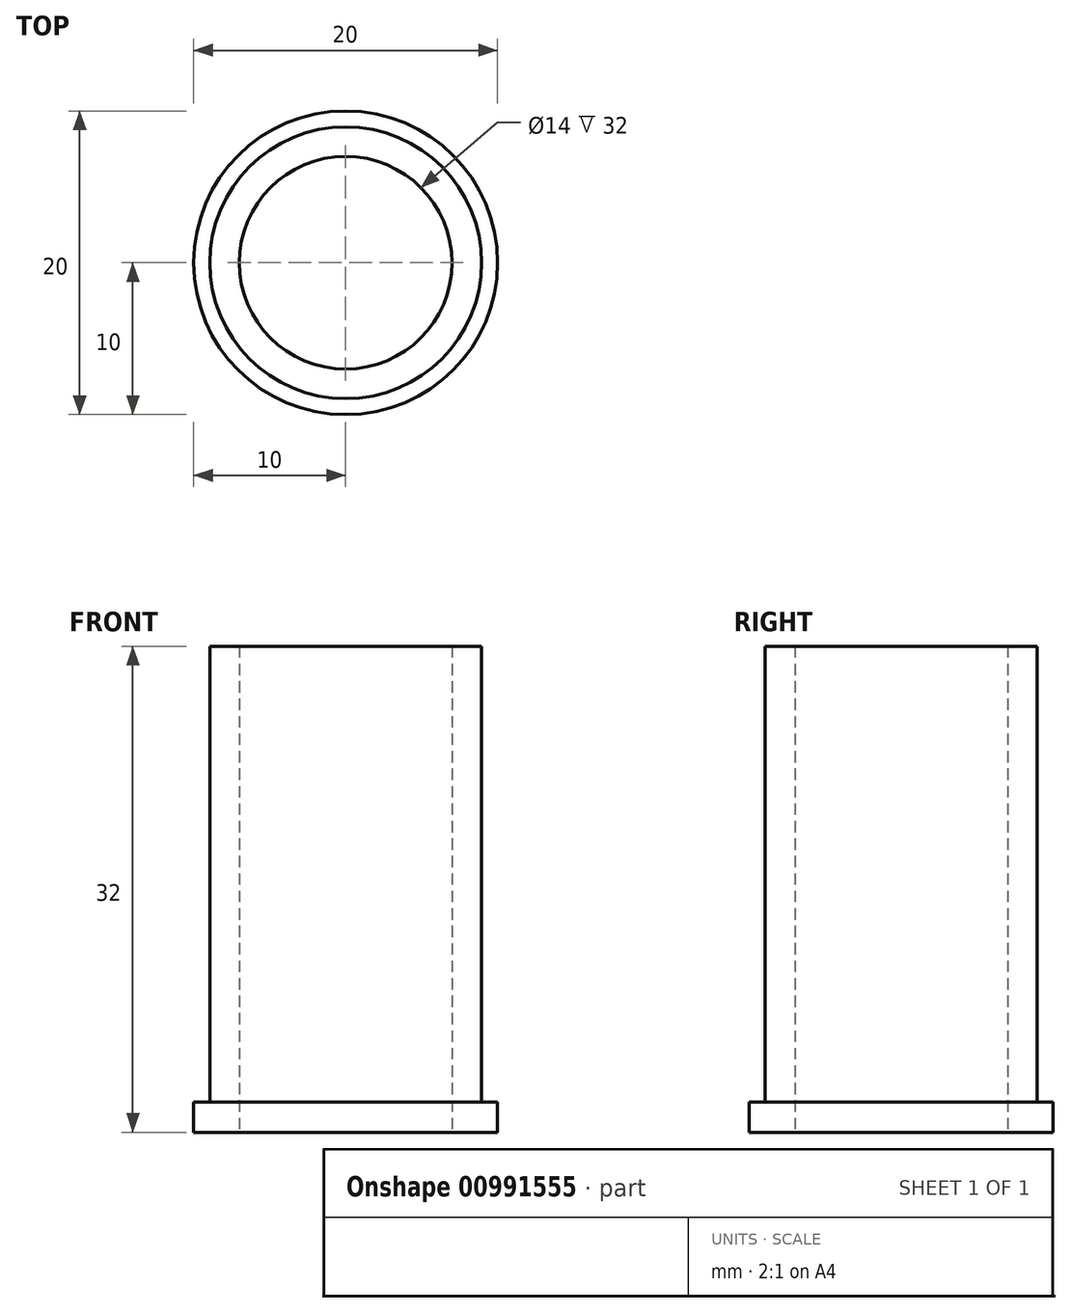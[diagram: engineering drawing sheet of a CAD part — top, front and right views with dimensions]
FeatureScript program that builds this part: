
annotation { "Feature Type Name" : "Feature", "Feature Type Description" : "" }
export const myFeature = defineFeature(function(context is Context, id is Id, definition is map)
    precondition{}
    {
        {
            var Q0;
            Q0=qCreatedBy(makeId("Top.planeOp"),FACE);
            var sketch = newSketch(context, id + "F0", { "sketchPlane" : qUnion([Q0]), "disableImprinting" : false});
            skCircle(sketch, "E0", {"center": v(0, 0) * mm, "radius": 8.95 * mm});
            skCircle(sketch, "E1", {"center": v(0, 0) * mm, "radius": 7 * mm});
            skSolve(sketch);
        }
        {
            var Q0;
            Q0=makeQuery(id+"F0.imprint","IMPRINT",FACE,{"disambiguationData":[TD([[makeQuery(id+"F0.imprint","IMPRINT",EDGE,{"derivedFrom":sQuery(id+"F0.wireOp",EDGE,"E0")}),1.0]])]});
            extrude(context, id + "F1", {"entities" : qUnion([Q0]), "depth" : 30 * mm, "offsetDistance" : 25 * mm});
        }
        {
            var Q0;
            Q0=makeQuery(id+"F1.opExtrude","CAP_FACE",FACE,{"disambiguationData":[OSD([sQuery(id+"F0.wireOp",EDGE,"E0"),sQuery(id+"F0.wireOp",EDGE,"E1")])],"isStart":true});
            var sketch = newSketch(context, id + "F2", { "sketchPlane" : qUnion([Q0])});
            skCircle(sketch, "E2", {"center": v(0, 0) * mm, "radius": 7 * mm});
            skCircle(sketch, "E3", {"center": v(0, 0) * mm, "radius": 10 * mm});
            skSolve(sketch);
        }
        {
            var Q0;
            Q0=makeQuery(id+"F2.imprint","IMPRINT",FACE,{"disambiguationData":[TD([[makeQuery(id+"F2.imprint","IMPRINT",EDGE,{"derivedFrom":sQuery(id+"F2.wireOp",EDGE,"E3")}),1.0]])]});
            var Q1;
            Q1=makeQuery(id+"F2.imprint","IMPRINT",FACE,{"disambiguationData":[TD([[makeQuery(id+"F2.imprint","IMPRINT",EDGE,{"derivedFrom":sQuery(id+"F2.wireOp",EDGE,"E2")}),1.0]])]});
            extrude(context, id + "F3", {"entities" : qUnion([Q0, Q1]), "operationType" : NewBodyOperationType.ADD, "depth" : 2 * mm, "offsetDistance" : 25 * mm});
        }
    });
